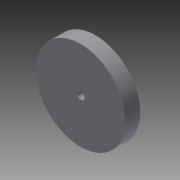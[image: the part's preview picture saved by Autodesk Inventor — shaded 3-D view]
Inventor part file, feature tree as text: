
AUTODESK INVENTOR PART (.ipt)
format: ipt  version: 2015 (Build 190159000, 159)  size: 101,888 bytes
history: native  units: mm
features: extrude x4, sketch x4, plane x1
ambient origin geometry x8: Origin, YZ Plane, XZ Plane, XY Plane, X Axis, Y Axis, Z Axis, Center Point
bodies: Solid1 (feature_tree)
feature tree (9):
  extrude  "Extrusion1"  Depth=5.0mm TaperAngle=0.0deg
  extrude  "Extrusion2"  Depth=10.0mm
  sketch  "Sketch3"  dims[d5=5.0mm d6=0.0mm d7=4.0mm]
  extrude  "Extrusion3"  Depth=5.0mm
  extrude  "Extrusion4"  Depth=3.0mm TaperAngle=0.0deg
  plane  "Work Plane1"
  sketch  "Sketch1"  dims[d0=47.5mm d1=5.0mm d2=0.0mm]
  sketch  "Sketch2"  dims[d3=10.0mm d4=10.0mm]
  sketch  "Sketch4"  dims[d8=5.0mm d9=3.0mm d10=0.0mm d11=3.0mm d12=0.0mm]
